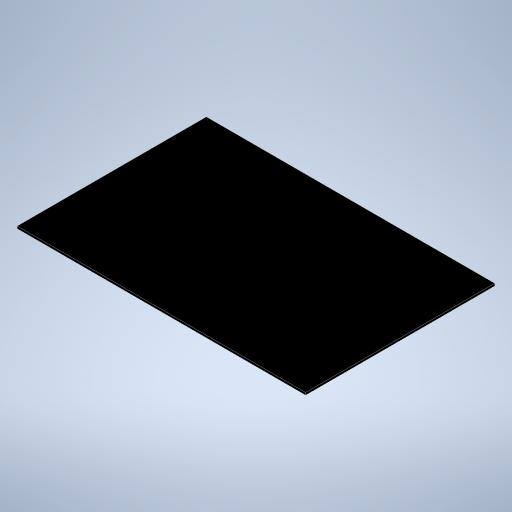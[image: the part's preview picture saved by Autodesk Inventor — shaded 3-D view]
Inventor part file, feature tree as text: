
AUTODESK INVENTOR PART (.ipt)
format: ipt  version: 2023 (Build 270158000, 158)  size: 214,016 bytes
history: native  units: mm
features: other x1, extrude x1, sketch x1
ambient origin geometry x8: Origin, YZ Plane, XZ Plane, XY Plane, X Axis, Y Axis, Z Axis, Center Point
bodies: Body1 (feature_tree)
feature tree (3):
  other  "ソリッド1"
  extrude  "押し出し1"  Depth=610.0mm
  sketch  "スケッチ1"
